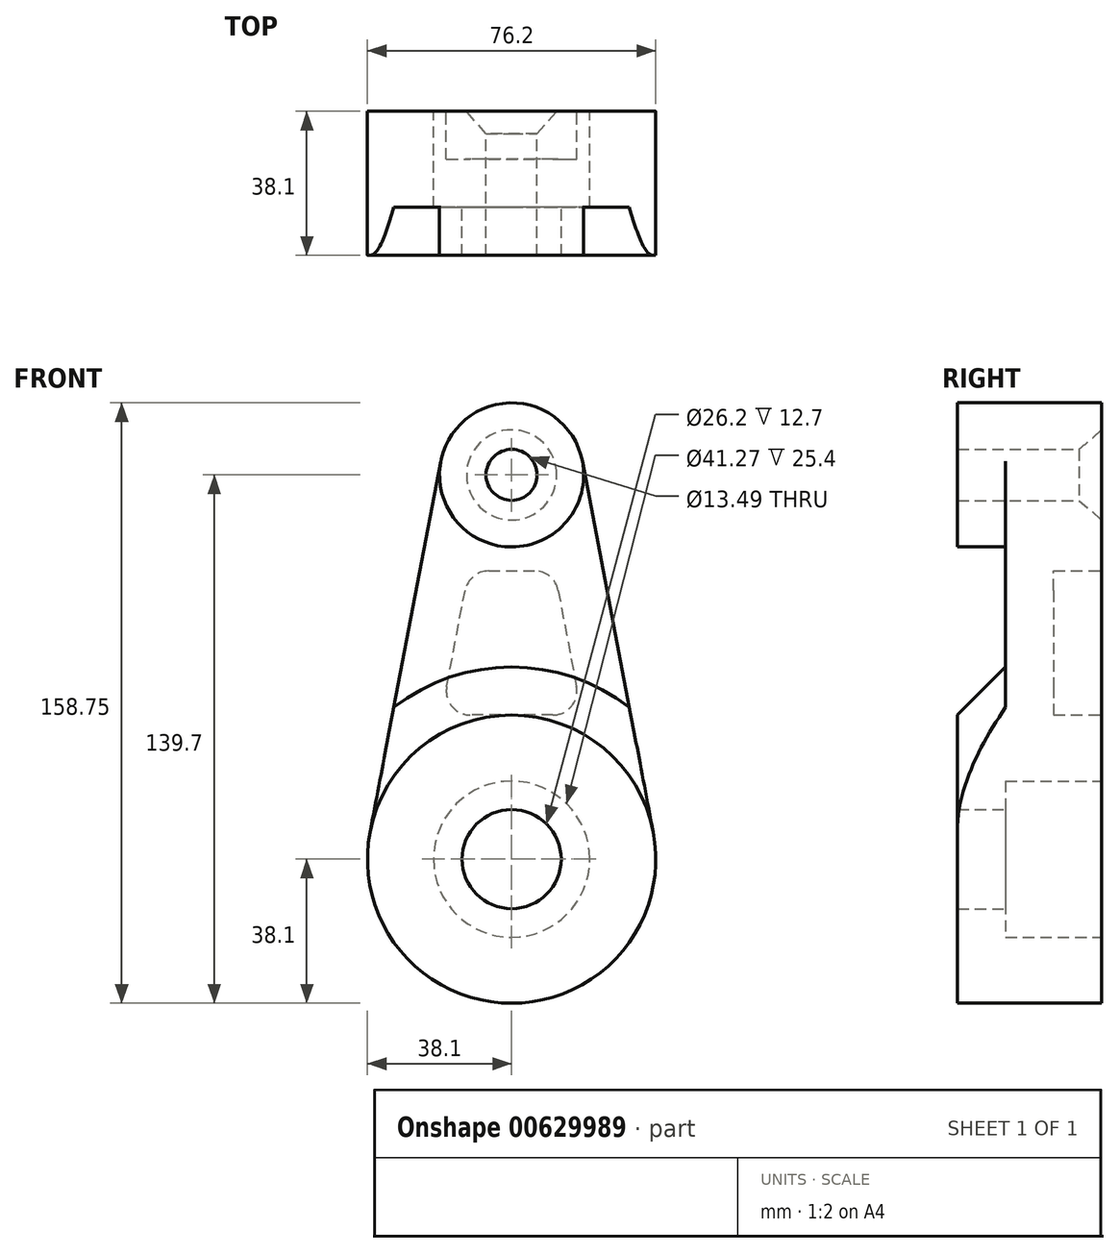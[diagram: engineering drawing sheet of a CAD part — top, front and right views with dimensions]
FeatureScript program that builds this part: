
annotation { "Feature Type Name" : "Feature", "Feature Type Description" : "" }
export const myFeature = defineFeature(function(context is Context, id is Id, definition is map)
    precondition{}
    {
        {
            var Q0;
            Q0=qCreatedBy(makeId("Front.planeOp"),FACE);
            var sketch = newSketch(context, id + "F0", { "sketchPlane" : qUnion([Q0])});
            skCircle(sketch, "E0", {"center": v(0, 0) * mm, "radius": 38.1 * mm});
            skCircle(sketch, "E1", {"center": v(0, 101.6) * mm, "radius": 19.05 * mm});
            skLineSegment(sketch, "E2", {"start": v(-18.71, 105.17) * mm, "end": v(-37.42, 7.14) * mm});
            skLineSegment(sketch, "E3", {"start": v(-37.42, 7.14) * mm, "end": v(-37.42, 7.14) * mm});
            skLineSegment(sketch, "E4", {"start": v(18.71, 105.17) * mm, "end": v(37.42, 7.14) * mm});
            skSolve(sketch);
        }
        {
            var Q0;
            Q0 = qSketchRegion(id + "F0", true);
            extrude(context, id + "F1", {"entities" : qUnion([Q0]), "depth" : 25.4 * mm, "offsetDistance" : 25.4 * mm});
        }
        {
            var Q0;
            {var subQ0=sQuery(id+"F0.wireOp",EDGE,"E0");var subQ1=makeQuery(id+"F0.imprint","INTERSECT",VERTEX,{"derivedFrom":[subQ0,sQuery(id+"F0.wireOp",EDGE,"E2")]});Q0=makeQuery(id+"F0.imprint","IMPRINT",FACE,{"disambiguationData":[TD([[makeQuery(id+"F0.imprint","IMPRINT",EDGE,{"disambiguationData":[TD([[subQ1,1.0]])],"derivedFrom":subQ0}),1.0]])]});}
            var Q1;
            {var subQ0=sQuery(id+"F0.wireOp",EDGE,"E1");var subQ1=makeQuery(id+"F0.imprint","INTERSECT",VERTEX,{"derivedFrom":[subQ0,sQuery(id+"F0.wireOp",EDGE,"E2")]});Q1=makeQuery(id+"F0.imprint","IMPRINT",FACE,{"disambiguationData":[TD([[makeQuery(id+"F0.imprint","IMPRINT",EDGE,{"disambiguationData":[TD([[subQ1,1.0]])],"derivedFrom":subQ0}),1.0]])]});}
            var Q2;
            Q2=sQuery(id+"F0.wireOp",EDGE,"E1");
            var Q3;
            Q3=sQuery(id+"F0.wireOp",EDGE,"E0");
            extrude(context, id + "F2", {"entities" : qUnion([Q0, Q1]), "operationType" : NewBodyOperationType.ADD, "surfaceEntities" : qUnion([Q2, Q3]), "depth" : 38.1 * mm, "offsetDistance" : 25.4 * mm});
        }
        {
            var Q0;
            {var subQ0=sQuery(id+"F0.wireOp",EDGE,"E0");Q0=makeQuery(id+"F2.boolean.opBoolean","INTERSECT",EDGE,{"derivedFrom":[makeQuery(id+"F1.opExtrude","CAP_FACE",FACE,{"disambiguationData":[OSD([subQ0,sQuery(id+"F0.wireOp",EDGE,"E1"),sQuery(id+"F0.wireOp",EDGE,"E2"),sQuery(id+"F0.wireOp",EDGE,"E4")])],"isStart":false}),makeQuery(id+"F2.opExtrude","SWEPT_FACE",FACE,{"disambiguationData":[OSD([subQ0])]})]});}
            chamfer(context, id + "F3", {"entities" : qUnion([Q0]), "width" : 12.7 * mm, "tangentPropagation" : true});
        }
        {
            var Q0;
            Q0=qCreatedBy(makeId("Front.planeOp"),FACE);
            var sketch = newSketch(context, id + "F4", { "sketchPlane" : qUnion([Q0])});
            skLineSegment(sketch, "E5", {"start": v(12.3, 71.04) * mm, "end": v(17.15, 45.64) * mm});
            skLineSegment(sketch, "E6", {"start": v(-17.15, 45.64) * mm, "end": v(-12.3, 71.04) * mm});
            skLineSegment(sketch, "E7", {"start": v(-6.06, 76.2) * mm, "end": v(6.06, 76.2) * mm});
            skLineSegment(sketch, "E8", {"start": v(10.9, 38.1) * mm, "end": v(-10.9, 38.1) * mm});
            skPoint(sketch, "E9.visualSharp", {"position": v(11.31, 76.2) * mm});
            skArc(sketch, "E9.filletArc", {"start": v(12.3, 71.04) * mm, "mid": v(10.1, 74.74) * mm, "end": v(6.06, 76.2) * mm});
            skPoint(sketch, "E10.visualSharp", {"position": v(-11.31, 76.2) * mm});
            skArc(sketch, "E10.filletArc", {"start": v(-6.06, 76.2) * mm, "mid": v(-10.1, 74.74) * mm, "end": v(-12.3, 71.04) * mm});
            skPoint(sketch, "E11.visualSharp", {"position": v(18.59, 38.1) * mm});
            skArc(sketch, "E11.filletArc", {"start": v(10.9, 38.1) * mm, "mid": v(15.8, 40.4) * mm, "end": v(17.15, 45.64) * mm});
            skPoint(sketch, "E12.visualSharp", {"position": v(-18.59, 38.1) * mm});
            skArc(sketch, "E12.filletArc", {"start": v(-17.15, 45.64) * mm, "mid": v(-15.8, 40.4) * mm, "end": v(-10.9, 38.1) * mm});
            skSolve(sketch);
        }
        {
            var Q0;
            Q0 = qSketchRegion(id + "F4", true);
            extrude(context, id + "F5", {"entities" : qUnion([Q0]), "operationType" : NewBodyOperationType.REMOVE, "depth" : 12.7 * mm, "offsetDistance" : 25.4 * mm});
        }
        {
            var Q0;
            Q0=makeQuery(id+"F1.opExtrude","CAP_FACE",FACE,{"disambiguationData":[OSD([sQuery(id+"F0.wireOp",EDGE,"E0"),sQuery(id+"F0.wireOp",EDGE,"E1"),sQuery(id+"F0.wireOp",EDGE,"E2"),sQuery(id+"F0.wireOp",EDGE,"E4")])],"isStart":true});
            var sketch = newSketch(context, id + "F6", { "sketchPlane" : qUnion([Q0])});
            skPoint(sketch, "E13", {"position": v(0, 0) * mm});
            skPoint(sketch, "E14", {"position": v(0, 101.6) * mm});
            skSolve(sketch);
        }
        {
            var Q0;
            Q0=sQuery(id+"F6.wireOp",VERTEX,"E13");
            var Q1;
            Q1=makeQuery(id+"F1.opExtrude","SWEPT_BODY",BODY,{"disambiguationData":[OSD([sQuery(id+"F0.wireOp",EDGE,"E0"),sQuery(id+"F0.wireOp",EDGE,"E1"),sQuery(id+"F0.wireOp",EDGE,"E2"),sQuery(id+"F0.wireOp",EDGE,"E4")])]});
            hole(context, id + "F7", {"style" : HoleStyle.C_BORE, "endStyle" : HoleEndStyle.THROUGH, "standardTappedOrClearance" : lookupTablePath({ "fit" : "Normal (ASME)", "standard" : "ANSI", "size" : "1", "type" : "Clearance" }), "standardBlindInLast" : lookupTablePath({ "fit" : "Free", "standard" : "ANSI", "size" : "1", "type" : "Clearance" }), "holeDiameter" : 26.2 * mm, "cBoreDiameter" : 41.27 * mm, "cBoreDepth" : 25.4 * mm, "majorDiameter" : 6.35 * mm, "isTappedThrough" : true, "tappedDepth" : 12.7 * mm, "tapClearance" : 3, "locations" : qUnion([Q0]), "scope" : qUnion([Q1])});
        }
        {
            var Q0;
            Q0=sQuery(id+"F6.wireOp",VERTEX,"E14");
            var Q1;
            Q1=makeQuery(id+"F1.opExtrude","SWEPT_BODY",BODY,{"disambiguationData":[OSD([sQuery(id+"F0.wireOp",EDGE,"E0"),sQuery(id+"F0.wireOp",EDGE,"E1"),sQuery(id+"F0.wireOp",EDGE,"E2"),sQuery(id+"F0.wireOp",EDGE,"E4")])]});
            hole(context, id + "F8", {"style" : HoleStyle.C_SINK, "endStyle" : HoleEndStyle.THROUGH, "standardTappedOrClearance" : lookupTablePath({ "fit" : "Normal (ASME)", "standard" : "ANSI", "size" : "1/2", "type" : "Clearance" }), "standardBlindInLast" : lookupTablePath({ "fit" : "Free", "standard" : "ANSI", "size" : "1/2", "type" : "Clearance" }), "holeDiameter" : 13.5 * mm, "cSinkDiameter" : 23.83 * mm, "cSinkAngle" : 82 * degree, "majorDiameter" : 6.35 * mm, "isTappedThrough" : true, "tappedDepth" : 12.7 * mm, "tapClearance" : 3, "locations" : qUnion([Q0]), "scope" : qUnion([Q1])});
        }
    });
